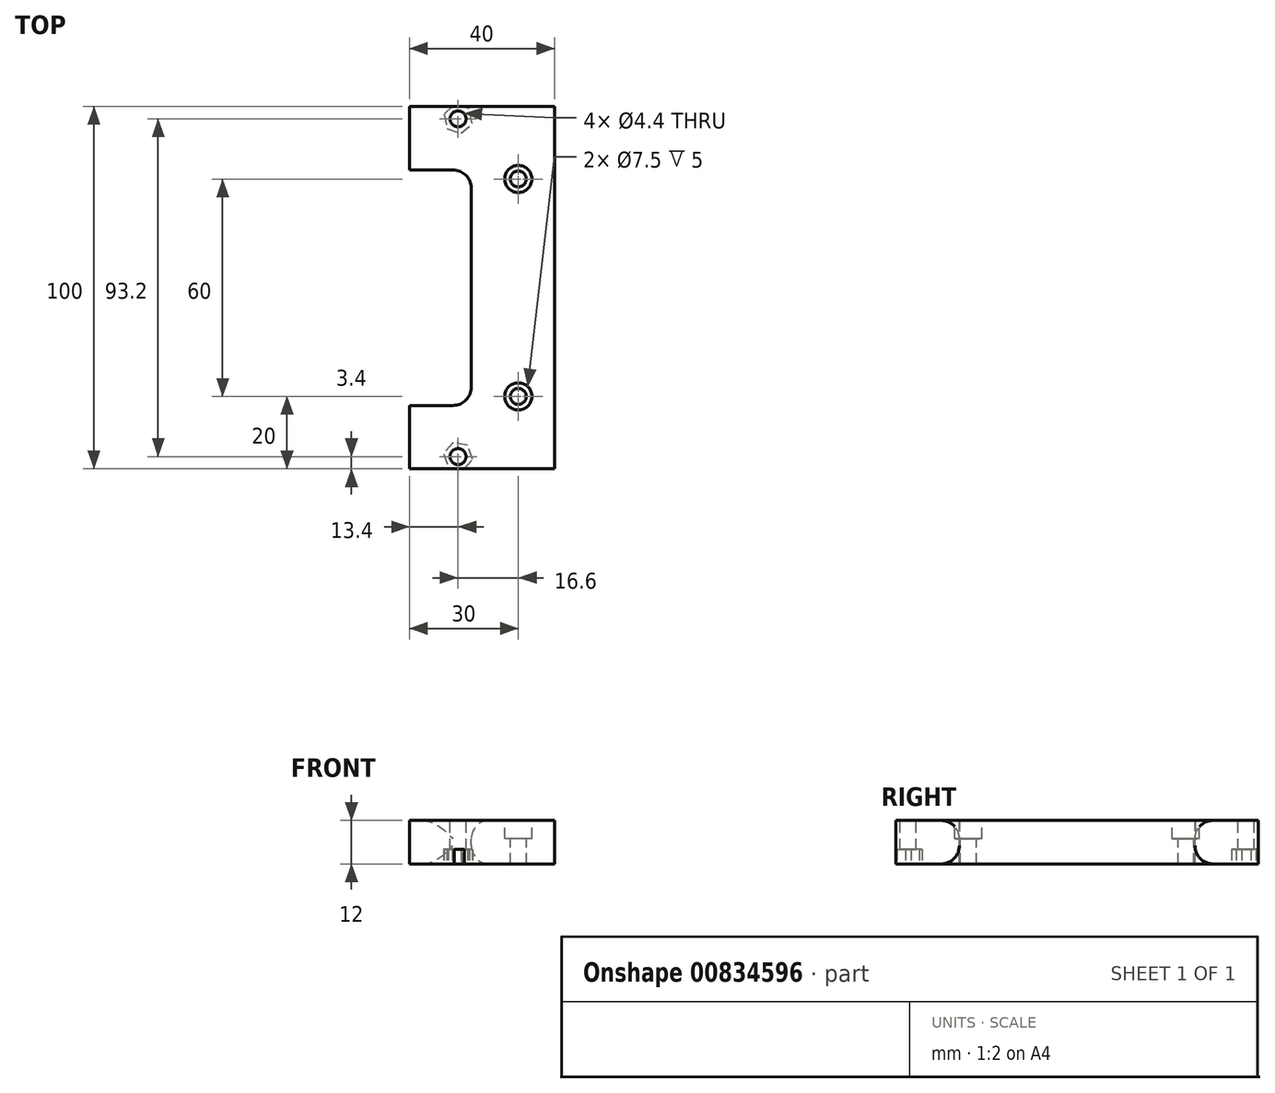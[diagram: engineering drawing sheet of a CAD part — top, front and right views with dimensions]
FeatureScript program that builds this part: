
annotation { "Feature Type Name" : "Feature", "Feature Type Description" : "" }
export const myFeature = defineFeature(function(context is Context, id is Id, definition is map)
    precondition{}
    {
        {
            var Q0;
            Q0=qCreatedBy(makeId("Top.planeOp"),FACE);
            var sketch = newSketch(context, id + "F0", { "sketchPlane" : qUnion([Q0])});
            skLineSegment(sketch, "E0.bottom", {"start": v(60, 50) * mm, "end": v(-60, 50) * mm});
            skLineSegment(sketch, "E0.top", {"start": v(60, -50) * mm, "end": v(-60, -50) * mm});
            skLineSegment(sketch, "E0.left", {"start": v(60, 50) * mm, "end": v(60, -50) * mm});
            skLineSegment(sketch, "E0.right", {"start": v(-60, 50) * mm, "end": v(-60, -50) * mm});
            skPoint(sketch, "E0.middle", {"position": v(0, 0) * mm});
            skCircle(sketch, "E1", {"center": v(-30, 30) * mm, "radius": 2.2 * mm});
            skCircle(sketch, "E2", {"center": v(-46.6, 46.6) * mm, "radius": 2.2 * mm});
            skCircle(sketch, "E3", {"center": v(-30, -30) * mm, "radius": 2.2 * mm});
            skCircle(sketch, "E4", {"center": v(30, -30) * mm, "radius": 2.2 * mm});
            skCircle(sketch, "E5", {"center": v(30, 30) * mm, "radius": 2.2 * mm});
            skCircle(sketch, "E6", {"center": v(-46.6, -46.6) * mm, "radius": 2.2 * mm});
            skCircle(sketch, "E7", {"center": v(46.6, -46.6) * mm, "radius": 2.2 * mm});
            skCircle(sketch, "E8", {"center": v(46.6, 46.6) * mm, "radius": 2.2 * mm});
            skSolve(sketch);
        }
        {
            var Q0;
            Q0=makeQuery(id+"F0.imprint","IMPRINT",FACE,{"disambiguationData":[TD([[makeQuery(id+"F0.imprint","IMPRINT",EDGE,{"derivedFrom":sQuery(id+"F0.wireOp",EDGE,"E0.bottom")}),1.0]])]});
            extrude(context, id + "F1", {"entities" : qUnion([Q0]), "oppositeDirection" : true, "depth" : 12 * mm, "offsetDistance" : 25 * mm});
        }
        {
            var Q0;
            Q0=makeQuery(id+"F1.opExtrude","CAP_FACE",FACE,{"disambiguationData":[OSD([sQuery(id+"F0.wireOp",EDGE,"E0.bottom"),sQuery(id+"F0.wireOp",EDGE,"E0.top"),sQuery(id+"F0.wireOp",EDGE,"E0.left"),sQuery(id+"F0.wireOp",EDGE,"E0.right"),sQuery(id+"F0.wireOp",EDGE,"E1"),sQuery(id+"F0.wireOp",EDGE,"E2"),sQuery(id+"F0.wireOp",EDGE,"E3"),sQuery(id+"F0.wireOp",EDGE,"E4"),sQuery(id+"F0.wireOp",EDGE,"E5"),sQuery(id+"F0.wireOp",EDGE,"E6"),sQuery(id+"F0.wireOp",EDGE,"E7"),sQuery(id+"F0.wireOp",EDGE,"E8")])],"isStart":true});
            var sketch = newSketch(context, id + "F2", { "sketchPlane" : qUnion([Q0])});
            skCircle(sketch, "E9", {"center": v(-30, 30) * mm, "radius": 3.75 * mm});
            skCircle(sketch, "E10", {"center": v(30, 30) * mm, "radius": 3.75 * mm});
            skCircle(sketch, "E11", {"center": v(30, -30) * mm, "radius": 3.75 * mm});
            skCircle(sketch, "E12", {"center": v(-30, -30) * mm, "radius": 3.75 * mm});
            skSolve(sketch);
        }
        {
            var Q0;
            Q0 = qSketchRegion(id + "F2", true);
            extrude(context, id + "F3", {"entities" : qUnion([Q0]), "operationType" : NewBodyOperationType.REMOVE, "oppositeDirection" : true, "depth" : 5 * mm, "offsetDistance" : 25 * mm});
        }
        {
            var Q0;
            Q0=makeQuery(id+"F1.opExtrude","CAP_FACE",FACE,{"disambiguationData":[OSD([sQuery(id+"F0.wireOp",EDGE,"E0.bottom"),sQuery(id+"F0.wireOp",EDGE,"E0.top"),sQuery(id+"F0.wireOp",EDGE,"E0.left"),sQuery(id+"F0.wireOp",EDGE,"E0.right"),sQuery(id+"F0.wireOp",EDGE,"E1"),sQuery(id+"F0.wireOp",EDGE,"E2"),sQuery(id+"F0.wireOp",EDGE,"E3"),sQuery(id+"F0.wireOp",EDGE,"E4"),sQuery(id+"F0.wireOp",EDGE,"E5"),sQuery(id+"F0.wireOp",EDGE,"E6"),sQuery(id+"F0.wireOp",EDGE,"E7"),sQuery(id+"F0.wireOp",EDGE,"E8")])],"isStart":false});
            var sketch = newSketch(context, id + "F4", { "sketchPlane" : qUnion([Q0])});
            skCircle(sketch, "E13.cCircle", {"center": v(-46.6, 46.6) * mm, "radius": 4.1 * mm, "construction": true});
            skLineSegment(sketch, "E13.0", {"start": v(-42.57, 47.35) * mm, "end": v(-43.94, 43.48) * mm});
            skLineSegment(sketch, "E13.1", {"start": v(-43.94, 43.48) * mm, "end": v(-47.97, 42.74) * mm});
            skLineSegment(sketch, "E13.2", {"start": v(-47.97, 42.74) * mm, "end": v(-50.63, 45.85) * mm});
            skLineSegment(sketch, "E13.3", {"start": v(-50.63, 45.85) * mm, "end": v(-49.26, 49.72) * mm});
            skLineSegment(sketch, "E13.4", {"start": v(-49.26, 49.72) * mm, "end": v(-45.23, 50.46) * mm});
            skLineSegment(sketch, "E13.5", {"start": v(-45.23, 50.46) * mm, "end": v(-42.57, 47.35) * mm});
            skCircle(sketch, "E14.cCircle", {"center": v(46.6, 46.6) * mm, "radius": 4.1 * mm, "construction": true});
            skLineSegment(sketch, "E14.0", {"start": v(50.03, 44.35) * mm, "end": v(46.36, 42.5) * mm});
            skLineSegment(sketch, "E14.1", {"start": v(46.36, 42.5) * mm, "end": v(42.94, 44.76) * mm});
            skLineSegment(sketch, "E14.2", {"start": v(42.94, 44.76) * mm, "end": v(43.17, 48.85) * mm});
            skLineSegment(sketch, "E14.3", {"start": v(43.17, 48.85) * mm, "end": v(46.84, 50.7) * mm});
            skLineSegment(sketch, "E14.4", {"start": v(46.84, 50.7) * mm, "end": v(50.26, 48.44) * mm});
            skLineSegment(sketch, "E14.5", {"start": v(50.26, 48.44) * mm, "end": v(50.03, 44.35) * mm});
            skCircle(sketch, "E15.cCircle", {"center": v(-46.6, -46.6) * mm, "radius": 4.1 * mm, "construction": true});
            skLineSegment(sketch, "E15.0", {"start": v(-45.75, -42.59) * mm, "end": v(-42.7, -45.33) * mm});
            skLineSegment(sketch, "E15.1", {"start": v(-42.7, -45.33) * mm, "end": v(-43.55, -49.34) * mm});
            skLineSegment(sketch, "E15.2", {"start": v(-43.55, -49.34) * mm, "end": v(-47.45, -50.61) * mm});
            skLineSegment(sketch, "E15.3", {"start": v(-47.45, -50.61) * mm, "end": v(-50.5, -47.87) * mm});
            skLineSegment(sketch, "E15.4", {"start": v(-50.5, -47.87) * mm, "end": v(-49.65, -43.86) * mm});
            skLineSegment(sketch, "E15.5", {"start": v(-49.65, -43.86) * mm, "end": v(-45.75, -42.59) * mm});
            skCircle(sketch, "E16.cCircle", {"center": v(46.6, -46.6) * mm, "radius": 4.1 * mm, "construction": true});
            skLineSegment(sketch, "E16.0", {"start": v(47.54, -42.6) * mm, "end": v(50.53, -45.42) * mm});
            skLineSegment(sketch, "E16.1", {"start": v(50.53, -45.42) * mm, "end": v(49.59, -49.4) * mm});
            skLineSegment(sketch, "E16.2", {"start": v(49.59, -49.4) * mm, "end": v(45.66, -50.6) * mm});
            skLineSegment(sketch, "E16.3", {"start": v(45.66, -50.6) * mm, "end": v(42.67, -47.78) * mm});
            skLineSegment(sketch, "E16.4", {"start": v(42.67, -47.78) * mm, "end": v(43.61, -43.8) * mm});
            skLineSegment(sketch, "E16.5", {"start": v(43.61, -43.8) * mm, "end": v(47.54, -42.6) * mm});
            skSolve(sketch);
        }
        {
            var Q0;
            Q0 = qSketchRegion(id + "F4", true);
            extrude(context, id + "F5", {"entities" : qUnion([Q0]), "operationType" : NewBodyOperationType.REMOVE, "oppositeDirection" : true, "depth" : 4 * mm, "offsetDistance" : 25 * mm});
        }
        {
            var Q0;
            Q0=makeQuery(id+"F1.opExtrude","CAP_FACE",FACE,{"disambiguationData":[OSD([sQuery(id+"F0.wireOp",EDGE,"E0.bottom"),sQuery(id+"F0.wireOp",EDGE,"E0.top"),sQuery(id+"F0.wireOp",EDGE,"E0.left"),sQuery(id+"F0.wireOp",EDGE,"E0.right"),sQuery(id+"F0.wireOp",EDGE,"E1"),sQuery(id+"F0.wireOp",EDGE,"E2"),sQuery(id+"F0.wireOp",EDGE,"E3"),sQuery(id+"F0.wireOp",EDGE,"E4"),sQuery(id+"F0.wireOp",EDGE,"E5"),sQuery(id+"F0.wireOp",EDGE,"E6"),sQuery(id+"F0.wireOp",EDGE,"E7"),sQuery(id+"F0.wireOp",EDGE,"E8")])],"isStart":true});
            var sketch = newSketch(context, id + "F6", { "sketchPlane" : qUnion([Q0])});
            skLineSegment(sketch, "E17.bottom", {"start": v(60, -50) * mm, "end": v(-20, -50) * mm});
            skLineSegment(sketch, "E17.top", {"start": v(60, 50) * mm, "end": v(-20, 50) * mm});
            skLineSegment(sketch, "E17.left", {"start": v(60, -50) * mm, "end": v(60, 50) * mm});
            skLineSegment(sketch, "E17.right", {"start": v(-20, -50) * mm, "end": v(-20, 50) * mm});
            skSolve(sketch);
        }
        {
            var Q0;
            Q0 = qSketchRegion(id + "F6", true);
            extrude(context, id + "F7", {"entities" : qUnion([Q0]), "operationType" : NewBodyOperationType.REMOVE, "oppositeDirection" : true, "depth" : 25 * mm, "offsetDistance" : 25 * mm});
        }
        {
            var Q0;
            Q0=makeQuery(id+"F1.opExtrude","CAP_FACE",FACE,{"disambiguationData":[OSD([sQuery(id+"F0.wireOp",EDGE,"E0.bottom"),sQuery(id+"F0.wireOp",EDGE,"E0.top"),sQuery(id+"F0.wireOp",EDGE,"E0.left"),sQuery(id+"F0.wireOp",EDGE,"E0.right"),sQuery(id+"F0.wireOp",EDGE,"E1"),sQuery(id+"F0.wireOp",EDGE,"E2"),sQuery(id+"F0.wireOp",EDGE,"E3"),sQuery(id+"F0.wireOp",EDGE,"E4"),sQuery(id+"F0.wireOp",EDGE,"E5"),sQuery(id+"F0.wireOp",EDGE,"E6"),sQuery(id+"F0.wireOp",EDGE,"E7"),sQuery(id+"F0.wireOp",EDGE,"E8")])],"isStart":true});
            var sketch = newSketch(context, id + "F8", { "sketchPlane" : qUnion([Q0])});
            skLineSegment(sketch, "E18.bottom", {"start": v(-60, 32.5) * mm, "end": v(-43, 32.5) * mm});
            skLineSegment(sketch, "E18.top", {"start": v(-60, -32.5) * mm, "end": v(-43, -32.5) * mm});
            skLineSegment(sketch, "E18.left", {"start": v(-60, 32.5) * mm, "end": v(-60, -32.5) * mm});
            skLineSegment(sketch, "E18.right", {"start": v(-43, 32.5) * mm, "end": v(-43, -32.5) * mm});
            skSolve(sketch);
        }
        {
            var Q0;
            Q0 = qSketchRegion(id + "F8", true);
            extrude(context, id + "F9", {"entities" : qUnion([Q0]), "operationType" : NewBodyOperationType.REMOVE, "oppositeDirection" : true, "depth" : 25 * mm, "offsetDistance" : 25 * mm});
        }
        {
            var Q0;
            Q0=makeQuery(id+"F9.boolean.opBoolean","COPY",EDGE,{"derivedFrom":makeQuery(id+"F9.opExtrude","CAP_EDGE",EDGE,{"disambiguationData":[OSD([sQuery(id+"F8.wireOp",EDGE,"E18.bottom")])],"isStart":true})});
            var Q1;
            Q1=makeQuery(id+"F9.boolean.opBoolean","COPY",FACE,{"derivedFrom":makeQuery(id+"F9.opExtrude","SWEPT_FACE",FACE,{"disambiguationData":[OSD([sQuery(id+"F8.wireOp",EDGE,"E18.right")])]})});
            fillet(context, id + "F10", {"entities" : qUnion([Q0, Q1]), "radius" : 5 * mm, "tangentPropagation" : true, "allowEdgeOverflow" : false});
        }
    });
